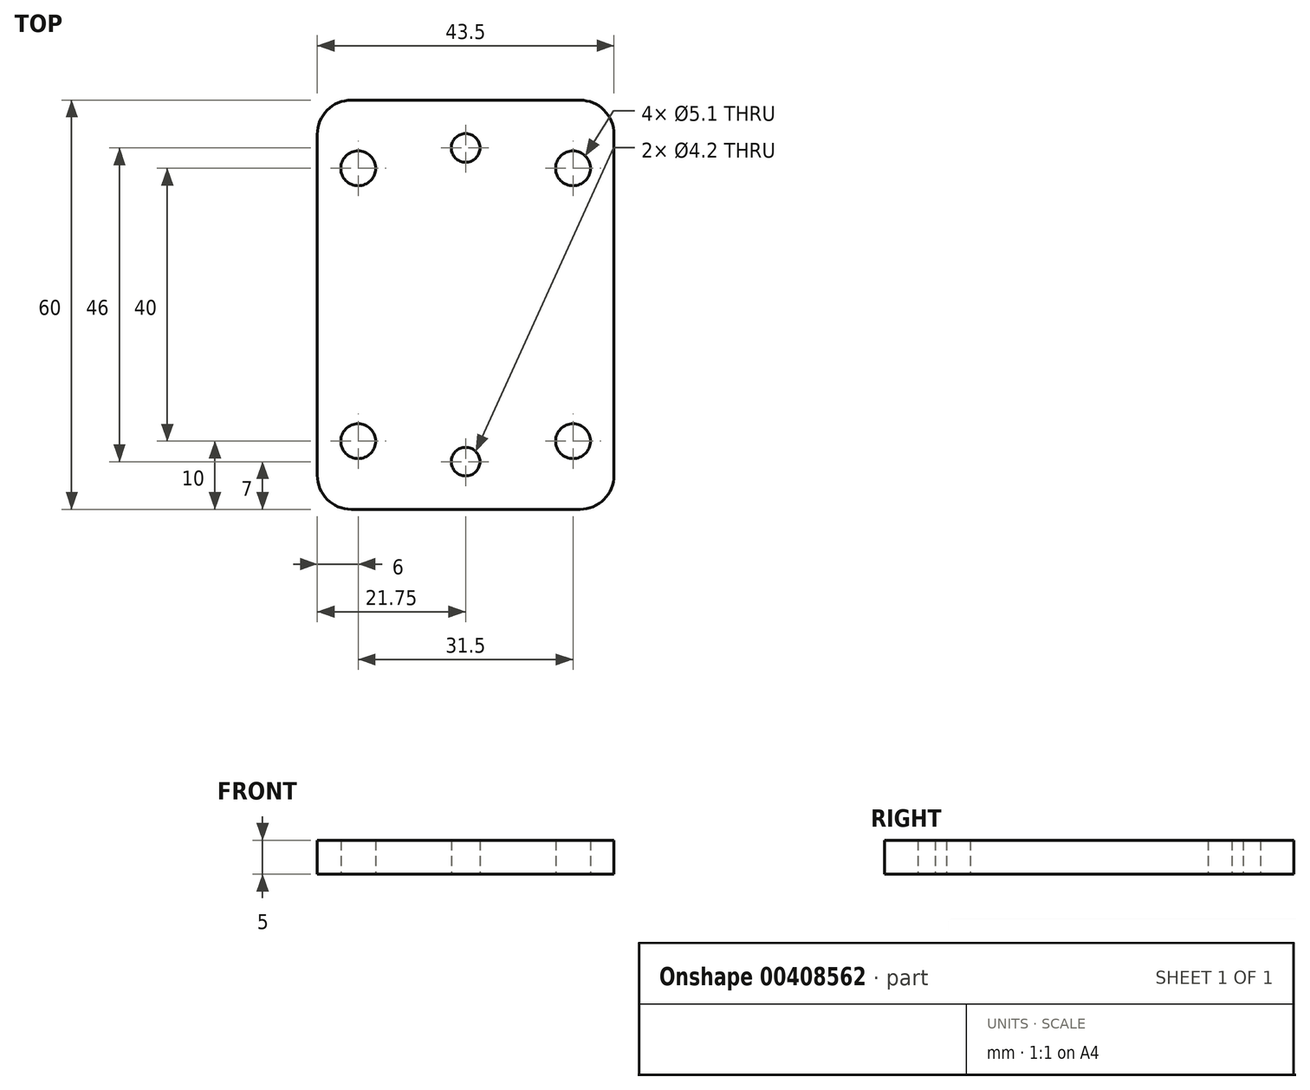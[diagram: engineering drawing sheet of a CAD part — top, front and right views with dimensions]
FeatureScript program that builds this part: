
annotation { "Feature Type Name" : "Feature", "Feature Type Description" : "" }
export const myFeature = defineFeature(function(context is Context, id is Id, definition is map)
    precondition{}
    {
        {
            var Q0;
            Q0=qCreatedBy(makeId("Top.planeOp"),FACE);
            var sketch = newSketch(context, id + "F0", { "sketchPlane" : qUnion([Q0])});
            skLineSegment(sketch, "E0.bottom", {"start": v(16.75, -30) * mm, "end": v(-16.75, -30) * mm});
            skLineSegment(sketch, "E0.top", {"start": v(16.75, 30) * mm, "end": v(-16.75, 30) * mm});
            skLineSegment(sketch, "E0.left", {"start": v(21.75, -25) * mm, "end": v(21.75, 25) * mm});
            skLineSegment(sketch, "E0.right", {"start": v(-21.75, -25) * mm, "end": v(-21.75, 25) * mm});
            skPoint(sketch, "E0.middle", {"position": v(0, 0) * mm});
            skPoint(sketch, "E1", {"position": v(0, 23) * mm});
            skPoint(sketch, "E2", {"position": v(0, -23) * mm});
            skPoint(sketch, "E3", {"position": v(-15.75, 20) * mm});
            skPoint(sketch, "E4", {"position": v(15.75, 20) * mm});
            skPoint(sketch, "E5", {"position": v(-15.75, -20) * mm});
            skPoint(sketch, "E6", {"position": v(15.75, -20) * mm});
            skCircle(sketch, "E7", {"center": v(-15.75, 20) * mm, "radius": 2.55 * mm});
            skCircle(sketch, "E8", {"center": v(0, 23) * mm, "radius": 2.1 * mm});
            skCircle(sketch, "E9", {"center": v(15.75, 20) * mm, "radius": 2.55 * mm});
            skCircle(sketch, "E10", {"center": v(15.75, -20) * mm, "radius": 2.55 * mm});
            skCircle(sketch, "E11", {"center": v(0, -23) * mm, "radius": 2.1 * mm});
            skCircle(sketch, "E12", {"center": v(-15.75, -20) * mm, "radius": 2.55 * mm});
            skPoint(sketch, "E13.visualSharp", {"position": v(-21.75, 30) * mm});
            skArc(sketch, "E13.filletArc", {"start": v(-16.75, 30) * mm, "mid": v(-20.29, 28.54) * mm, "end": v(-21.75, 25) * mm});
            skPoint(sketch, "E14.visualSharp", {"position": v(21.75, 30) * mm});
            skArc(sketch, "E14.filletArc", {"start": v(21.75, 25) * mm, "mid": v(20.29, 28.54) * mm, "end": v(16.75, 30) * mm});
            skPoint(sketch, "E15.visualSharp", {"position": v(21.75, -30) * mm});
            skArc(sketch, "E15.filletArc", {"start": v(16.75, -30) * mm, "mid": v(20.29, -28.54) * mm, "end": v(21.75, -25) * mm});
            skPoint(sketch, "E16.visualSharp", {"position": v(-21.75, -30) * mm});
            skArc(sketch, "E16.filletArc", {"start": v(-21.75, -25) * mm, "mid": v(-20.29, -28.54) * mm, "end": v(-16.75, -30) * mm});
            skSolve(sketch);
        }
        {
            var Q0;
            Q0=makeQuery(id+"F0.imprint","IMPRINT",FACE,{"disambiguationData":[TD([[makeQuery(id+"F0.imprint","IMPRINT",EDGE,{"derivedFrom":sQuery(id+"F0.wireOp",EDGE,"E0.bottom")}),-1.0]])]});
            extrude(context, id + "F1", {"entities" : qUnion([Q0]), "depth" : 5 * mm});
        }
    });
